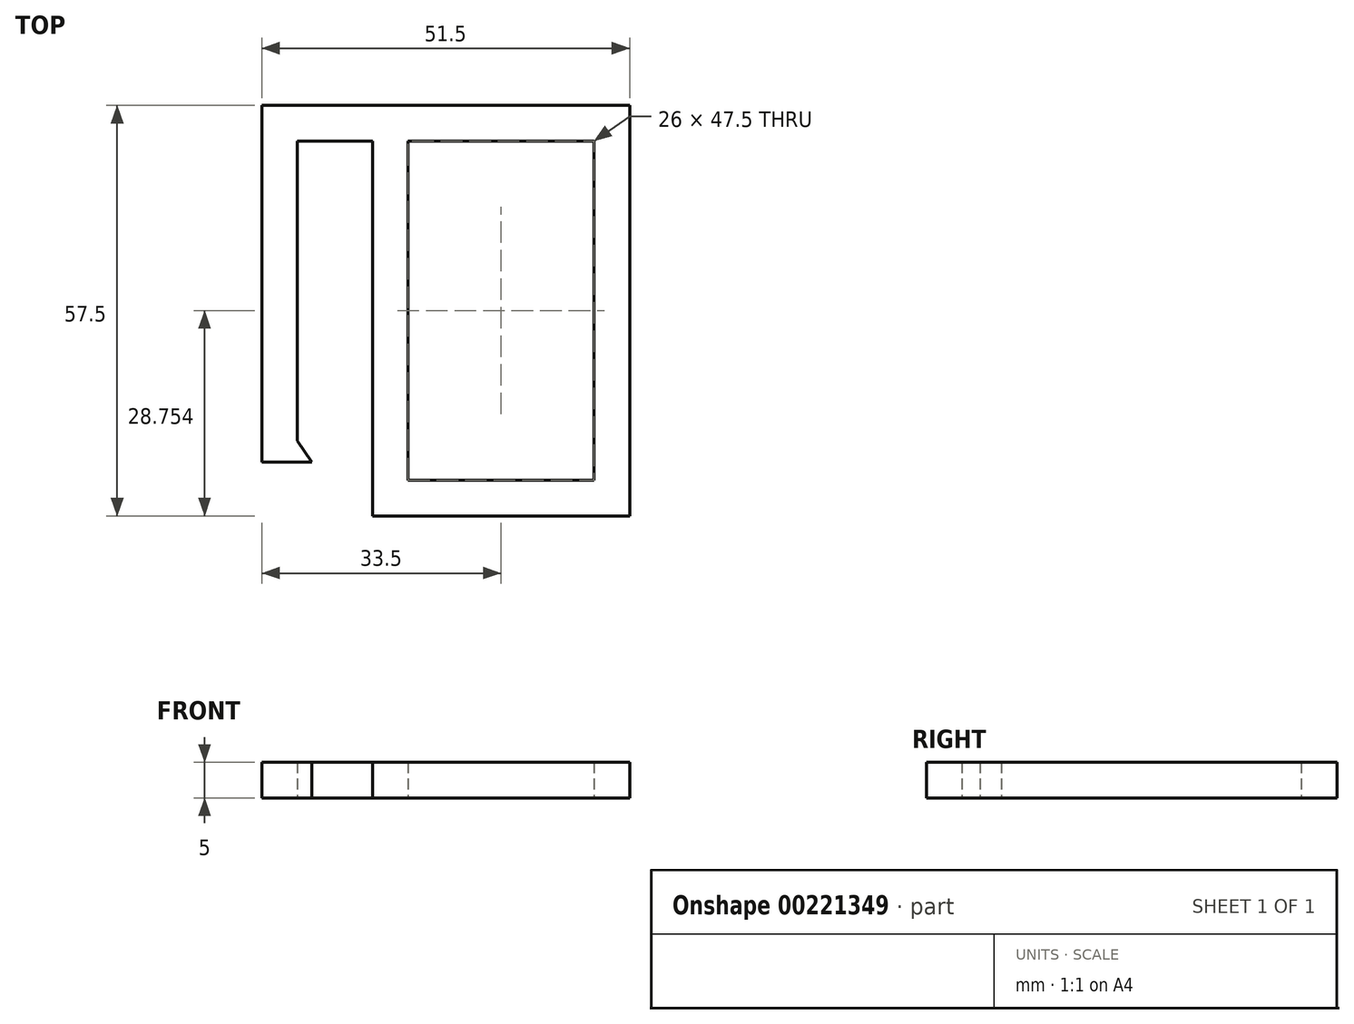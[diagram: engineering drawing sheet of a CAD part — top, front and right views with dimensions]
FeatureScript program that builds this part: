
annotation { "Feature Type Name" : "Feature", "Feature Type Description" : "" }
export const myFeature = defineFeature(function(context is Context, id is Id, definition is map)
    precondition{}
    {
        {
            var Q0;
            Q0=qCreatedBy(makeId("Top.planeOp"),FACE);
            var sketch = newSketch(context, id + "F0", { "sketchPlane" : qUnion([Q0])});
            skLineSegment(sketch, "E0", {"start": v(-20.5, 15.3) * mm, "end": v(-20.5, 65.3) * mm});
            skLineSegment(sketch, "E1", {"start": v(-20.5, 65.3) * mm, "end": v(31, 65.3) * mm});
            skLineSegment(sketch, "E2", {"start": v(31, 65.3) * mm, "end": v(31, 7.8) * mm});
            skLineSegment(sketch, "E3", {"start": v(31, 7.8) * mm, "end": v(-5, 7.8) * mm});
            skLineSegment(sketch, "E4", {"start": v(-5, 7.8) * mm, "end": v(-5, 60.3) * mm});
            skLineSegment(sketch, "E5", {"start": v(-5, 60.3) * mm, "end": v(-15.5, 60.3) * mm});
            skLineSegment(sketch, "E6", {"start": v(-15.5, 60.3) * mm, "end": v(-15.5, 18.3) * mm});
            skLineSegment(sketch, "E7", {"start": v(-13.5, 15.3) * mm, "end": v(-20.5, 15.3) * mm});
            skLineSegment(sketch, "E8", {"start": v(0, 60.3) * mm, "end": v(26, 60.3) * mm});
            skLineSegment(sketch, "E9", {"start": v(26, 60.3) * mm, "end": v(26, 12.8) * mm});
            skLineSegment(sketch, "E10", {"start": v(26, 12.8) * mm, "end": v(0, 12.8) * mm});
            skLineSegment(sketch, "E11", {"start": v(0, 12.8) * mm, "end": v(0, 60.3) * mm});
            skLineSegment(sketch, "E12", {"start": v(-15.5, 18.3) * mm, "end": v(-13.5, 15.3) * mm});
            skSolve(sketch);
        }
        {
            var Q0;
            Q0=makeQuery(id+"F0.imprint","IMPRINT",FACE,{"disambiguationData":[TD([[makeQuery(id+"F0.imprint","IMPRINT",EDGE,{"derivedFrom":sQuery(id+"F0.wireOp",EDGE,"E0")}),-1.0]])]});
            extrude(context, id + "F1", {"entities" : qUnion([Q0]), "depth" : 5 * mm});
        }
    });
